# Revit family: AIRTECNICS_AIR CURTAIN_ROTOWIND_ELECTRICAL HEATED (E) - (On Top Mounting)_0
name_source: partatom
category: Mechanical Equipment
revit_build: Autodesk Revit 2016 (Build: 20150714_1515(x64)
units: mm (PartAtom-declared; Revit-internal decimal feet)

## family parameters
Always vertical = Yes
Cut with Voids When Loaded = No
OmniClass Number = 23.75.70.21.17
OmniClass Title = Air Curtains
Part Type = Normal
Room Calculation Point = No
Round Connector Dimension = Use Diameter
Shared = No
Work Plane-Based = No

## types (2) — shared parameters
BIMETRICAL = http://www.bimetrical.com
BIMETRICAL Category = Coil
Cable = CB7
Family Version = 1.0
Fans Stage = 5
Frequency = 50 Hz
G = Yes
IfcExportAs = IfcCoilType
IfcExportType = ELECTRICHEATINGCOIL
Manufacturer = AIRTECNICS
Model = Air curtain Rotowind G (E)
Name_Lookup_Data = ROTOWIND_(E)_Data_Lookup
Name_Lookup_Electrical = ROTOWIND_(E)_Electrical_Lookup
Name_Lookup_Ref = ROTOWIND_(E)_Ref_Lookup
Remote Control = IR-AIR
Review Date = 01/19
Revit Version = Revit 2016 - English
Type Comments = Specially designed to be installed in all type of revolving doors. Two possible layouts, tailored dimensions.
Self-supporting casing construction made of galvanized steel plate, finished in structural epoxy-polyester painting white colour RAL9016 as standard. Other colours or stainless steel are available on request. 
Large faceted inlet grille avoiding intensive maintenance. 
Circular anodized aluminium outlet vanes, airfoil shaped.
Double-inlet centrifugal fans driven by an external rotor motor and low noise level. 5-speed selector. EC models assembled with very low consumption efficiency fans. 
“P” type with water heated coil. “E” type with electrical shielded elements, three stages with integrated regulation. “A” type without heating, air only. Optional expansion DX coil.
Includes Plug&Play control with 7m RJ45 cable and infrared remote control. Optional: Clever control (programmable, automatic, intelligent, energy saving, Modbus RTU for BMS…)
Type Image = <None>
URL = https://www.airtecnics.com
URL_Datasheet = https://www.airtecnics.com
URL_Manufacturer = https://www.airtecnics.com

## per-type parameters (varying)
| type | EC |
| ROTOWIND G E - (On Top Mounting) | No |
| ROTOWIND ECG E - (On Top Mounting) | Yes |
